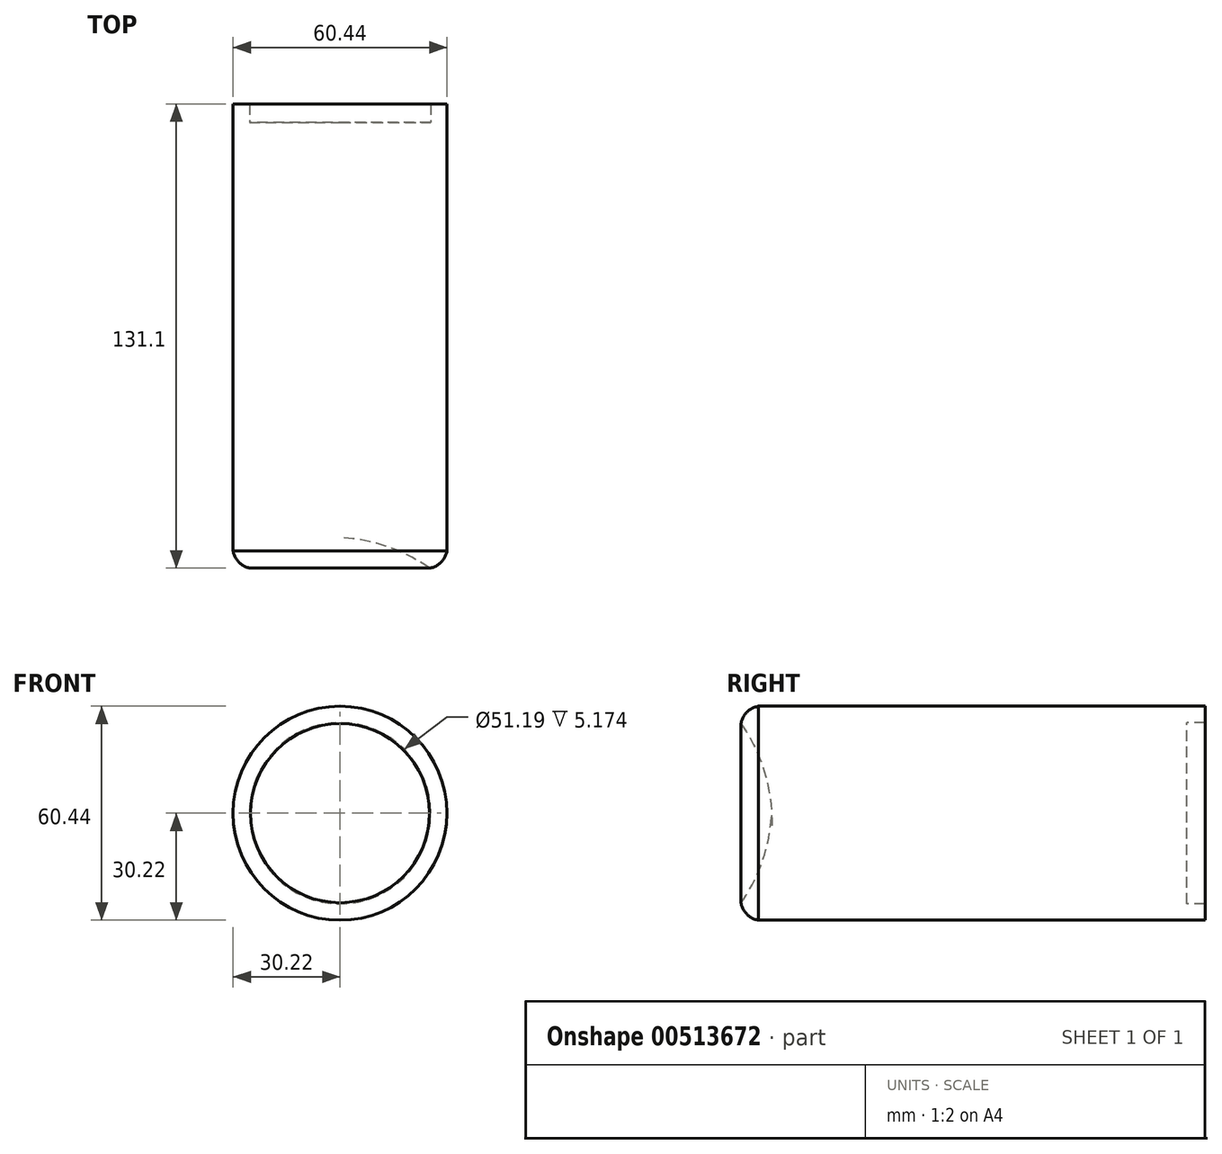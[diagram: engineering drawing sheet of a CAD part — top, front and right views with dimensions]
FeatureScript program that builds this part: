
annotation { "Feature Type Name" : "Feature", "Feature Type Description" : "" }
export const myFeature = defineFeature(function(context is Context, id is Id, definition is map)
    precondition{}
    {
        {
            var Q0;
            Q0=qCreatedBy(makeId("Top.planeOp"),FACE);
            var sketch = newSketch(context, id + "F0", { "sketchPlane" : qUnion([Q0])});
            skArc(sketch, "E0", {"start": v(25.29, -75.44) * mm, "mid": v(13.26, -69.33) * mm, "end": v(0, -66.8) * mm});
            skArc(sketch, "E1", {"start": v(25.29, -75.44) * mm, "mid": v(28.55, -73.77) * mm, "end": v(30.22, -70.5) * mm});
            skLineSegment(sketch, "E2", {"start": v(30.22, -70.5) * mm, "end": v(30.22, 55.66) * mm});
            skLineSegment(sketch, "E3", {"start": v(30.22, 55.66) * mm, "end": v(25.6, 55.66) * mm});
            skLineSegment(sketch, "E4", {"start": v(0, -66.8) * mm, "end": v(0, 76.02) * mm, "construction": true});
            skLineSegment(sketch, "E5", {"start": v(25.6, 55.66) * mm, "end": v(25.6, 50.48) * mm});
            skLineSegment(sketch, "E6", {"start": v(25.6, 50.48) * mm, "end": v(0, 50.48) * mm});
            skLineSegment(sketch, "E7", {"start": v(0, 50.48) * mm, "end": v(0, -73.89) * mm});
            skSolve(sketch);
        }
        {
            var Q0;
            {var subQ0=sQuery(id+"F0.wireOp",EDGE,"E0");Q0=makeQuery(id+"F0.imprint","IMPRINT",FACE,{"disambiguationData":[TD([[makeQuery(id+"F0.imprint","IMPRINT",EDGE,{"derivedFrom":subQ0}),-1.0]])]});}
            var Q1;
            Q1=sQuery(id+"F0.wireOp",EDGE,"E4");
            var Q2;
            Q2=sQuery(id+"F0.wireOp",EDGE,"E4");
            revolve(context, id + "F1", {"entities" : qUnion([Q0]), "surfaceEntities" : qUnion([Q1]), "axis" : qUnion([Q2]), "revolveType" : RevolveType.FULL});
        }
    });
